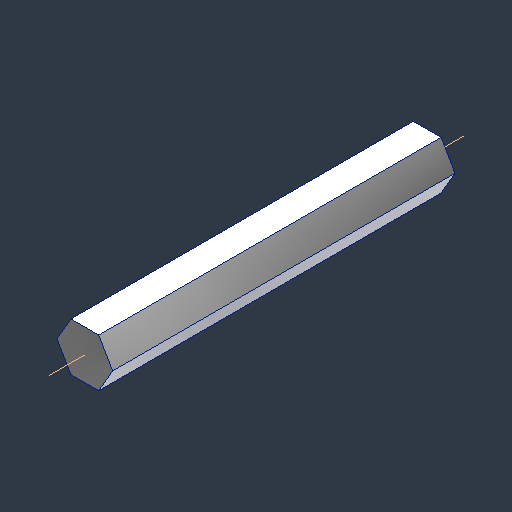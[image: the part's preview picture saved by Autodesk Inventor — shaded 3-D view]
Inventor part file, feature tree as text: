
AUTODESK INVENTOR PART (.ipt)
format: ipt  version: 2024.3 (Build 283343000, 343)  size: 98,304 bytes
history: native  units: mm (DEFAULTED — no unit token found)
features: extrude x1, sketch x1
ambient origin geometry x8: Origin, YZ Plane, XZ Plane, XY Plane, X Axis, Y Axis, Z Axis, Center Point
bodies: Solid1 (feature_tree)
feature tree (2):
  extrude  "Extrusion1"  Depth=90.17mm TaperAngle=0.0deg
  sketch  "Sketch2"  dims[d0=12.7mm d1=90.17mm d2=0.0mm]
